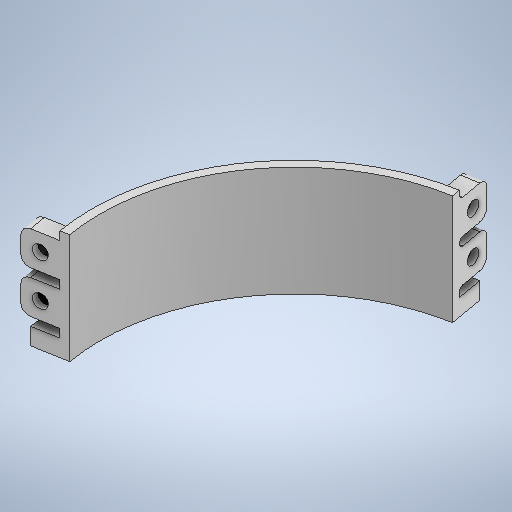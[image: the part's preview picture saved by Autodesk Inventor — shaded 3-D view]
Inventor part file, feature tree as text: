
AUTODESK INVENTOR PART (.ipt)
format: ipt  version: 2025 (Build 290162000, 162)  size: 535,040 bytes
history: native  units: in
note: dims shown in document units (in); Inventor stores cm internally (conversion verified against a paired STEP export)
features: sketch x14, extrude x11, other x3, hole x2, fillet x1
ambient origin geometry x8: Origin, YZ Plane, XZ Plane, XY Plane, X Axis, Y Axis, Z Axis, Center Point
bodies: Body1 (feature_tree)
feature tree (31):
  other  "Cylinder.ipt"
  extrude  "Extrusion1"  Depth=0.3937in
  extrude  "Extrusion2"  Depth=0.3937in TaperAngle=0.0deg
  sketch  "Sketch3"  dims[d15=0.1969in d16=0.0in d17=10.6299in]
  extrude  "Extrusion3"  Depth=10.6299in
  extrude  "Extrusion5"  Depth=0.1969in TaperAngle=0.0deg
  sketch  "Sketch6"  dims[d20=3.937in d22=360.0deg d24=0.1969in d25=0.0in]
  extrude  "Extrusion6"  Depth=10.6299in
  extrude  "Extrusion7"  Depth=0.3346in
  extrude  "Extrusion8"  Depth=0.1969in TaperAngle=0.0deg
  extrude  "Extrusion9"  TaperAngle=0.0deg  [1 undecoded]
  extrude  "Bolt Bracket"  Depth=10.0394in
  hole  "Bolt Hole Bore"  [1 undecoded]
  extrude  "Nut Bracket"  TaperAngle=0.0deg  [1 undecoded]
  fillet  "Fillet1"  Radius=0.8858in
  extrude  "Extrusion12"  Depth=0.7874in
  hole  "Hole2"  [1 undecoded]
  other  "Solid12::Cylinder.ipt"
  other  "TaggingFeature1"
  sketch  "Sketch1"  dims[d0=0.3937in d2=10.2362in]
  sketch  "Sketch2"  dims[d7=11.2205in d8=10.6299in]
  sketch  "Sketch5"  dims[d18=0.2953in d19=0.3346in]
  sketch  "Sketch Circular Pattern1"  dims[d3=0.0in d4=0.0in d5=0.3937in d6=0.0in]
  sketch  "Sketch Circular Pattern2"  dims[d9=10.6299in d10=0.1969in d11=0.0in]
  sketch  "Sketch7"  dims[d27=3.937in d29=360.0deg d31=0.0in d32=0.0in]
  sketch  "Sketch8"  dims[d33=2.1654in d34=0.0in d35=10.0394in]
  sketch  "Sketch9"  dims[d36=10.6299in d37=0.1969in]
  sketch  "Sketch10"  dims[d38=0.0687in d39=0.0in d40=0.0in d41=0.8858in]
  sketch  "Sketch11"  dims[d42=0.7874in d43=0.7874in]
  sketch  "Sketch12"  dims[d44=0.1969in d45=0.1969in]
  sketch  "Sketch13"  dims[d46=0.7874in d47=0.1969in d48=0.3937in d49=0.0in d50=0.1969in d51=0.8858in d52=0.7874in d53=0.7874in d54=0.1969in d55=0.1969in d56=0.7874in d57=0.1969in d58=0.3937in d59=0.0in d60=0.3937in d61=0.3937in d62=0.3937in d63=0.3937in d64=0.3228in d65=0.2362in d66=0.5197in d67=0.2362in d68=90.0deg d69=0.315in d70=0.8108in d71=0.0984in d72=0.3937in d73=0.3937in d74=0.3937in d75=0.3937in d76=0.2362in d77=0.0in d78=0.3937in d79=0.3937in d80=0.3937in d81=0.3228in d82=0.2362in d83=0.5197in d84=0.2362in d85=90.0deg d86=0.315in d87=0.8108in]
note: 4 required parameter values undecoded (feature->parameter linkage not recoverable at this tier; creation-order binding heuristic only, values carry confidence <= 0.55)
